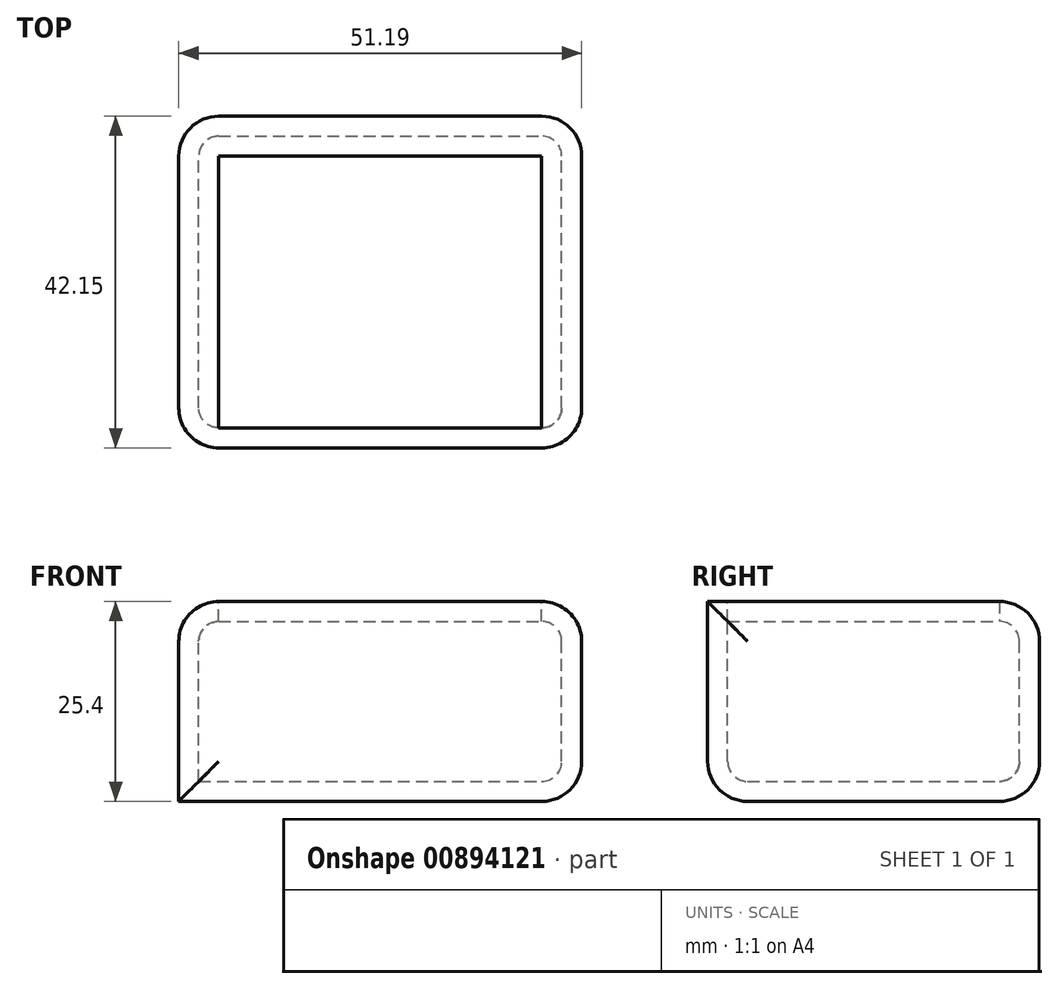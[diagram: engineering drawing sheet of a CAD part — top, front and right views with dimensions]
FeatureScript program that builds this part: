
annotation { "Feature Type Name" : "Feature", "Feature Type Description" : "" }
export const myFeature = defineFeature(function(context is Context, id is Id, definition is map)
    precondition{}
    {
        {
            var Q0;
            Q0=qCreatedBy(makeId("Top.planeOp"),FACE);
            var sketch = newSketch(context, id + "F0", { "sketchPlane" : qUnion([Q0])});
            skLineSegment(sketch, "E0.bottom", {"start": v(-27.28, -21.54) * mm, "end": v(23.9, -21.54) * mm});
            skLineSegment(sketch, "E0.top", {"start": v(-27.28, 20.6) * mm, "end": v(23.9, 20.6) * mm});
            skLineSegment(sketch, "E0.left", {"start": v(-27.28, -21.54) * mm, "end": v(-27.28, 20.6) * mm});
            skLineSegment(sketch, "E0.right", {"start": v(23.9, -21.54) * mm, "end": v(23.9, 20.6) * mm});
            skSolve(sketch);
        }
        {
            var Q0;
            Q0 = qSketchRegion(id + "F0", true);
            extrude(context, id + "F1", {"entities" : qUnion([Q0]), "depth" : 25.4 * mm, "offsetDistance" : 25.4 * mm});
        }
        {
            var Q0;
            Q0=makeQuery(id+"F1.opExtrude","CAP_EDGE",EDGE,{"disambiguationData":[OSD([sQuery(id+"F0.wireOp",EDGE,"E0.top")])],"isStart":false});
            var Q1;
            Q1=makeQuery(id+"F1.opExtrude","CAP_EDGE",EDGE,{"disambiguationData":[OSD([sQuery(id+"F0.wireOp",EDGE,"E0.left")])],"isStart":false});
            var Q2;
            Q2=makeQuery(id+"F1.opExtrude","CAP_EDGE",EDGE,{"disambiguationData":[OSD([sQuery(id+"F0.wireOp",EDGE,"E0.right")])],"isStart":false});
            var Q3;
            Q3=makeQuery(id+"F1.opExtrude","CAP_EDGE",EDGE,{"disambiguationData":[OSD([sQuery(id+"F0.wireOp",EDGE,"E0.right")])],"isStart":true});
            var Q4;
            Q4=makeQuery(id+"F1.opExtrude","SWEPT_EDGE",EDGE,{"disambiguationData":[OSD([sQuery(id+"F0.wireOp",EDGE,"E0.top"),sQuery(id+"F0.wireOp",EDGE,"E0.right")])]});
            var Q5;
            Q5=makeQuery(id+"F1.opExtrude","SWEPT_EDGE",EDGE,{"disambiguationData":[OSD([sQuery(id+"F0.wireOp",EDGE,"E0.bottom"),sQuery(id+"F0.wireOp",EDGE,"E0.right")])]});
            var Q6;
            Q6=makeQuery(id+"F1.opExtrude","SWEPT_EDGE",EDGE,{"disambiguationData":[OSD([sQuery(id+"F0.wireOp",EDGE,"E0.top"),sQuery(id+"F0.wireOp",EDGE,"E0.left")])]});
            var Q7;
            Q7=makeQuery(id+"F1.opExtrude","CAP_EDGE",EDGE,{"disambiguationData":[OSD([sQuery(id+"F0.wireOp",EDGE,"E0.bottom")])],"isStart":true});
            var Q8;
            Q8=makeQuery(id+"F1.opExtrude","SWEPT_EDGE",EDGE,{"disambiguationData":[OSD([sQuery(id+"F0.wireOp",EDGE,"E0.bottom"),sQuery(id+"F0.wireOp",EDGE,"E0.left")])]});
            var Q9;
            Q9=makeQuery(id+"F1.opExtrude","CAP_EDGE",EDGE,{"disambiguationData":[OSD([sQuery(id+"F0.wireOp",EDGE,"E0.top")])],"isStart":true});
            fillet(context, id + "F2", {"entities" : qUnion([Q0, Q1, Q2, Q3, Q4, Q5, Q6, Q7, Q8, Q9]), "radius" : 5.08 * mm, "tangentPropagation" : true, "allowEdgeOverflow" : false});
        }
        {
            var Q0;
            Q0=makeQuery(id+"F1.opExtrude","CAP_FACE",FACE,{"disambiguationData":[OSD([sQuery(id+"F0.wireOp",EDGE,"E0.bottom"),sQuery(id+"F0.wireOp",EDGE,"E0.top"),sQuery(id+"F0.wireOp",EDGE,"E0.left"),sQuery(id+"F0.wireOp",EDGE,"E0.right")])],"isStart":false});
            shell(context, id + "F3", {"entities" : qUnion([Q0]), "thickness" : 2.54 * mm});
        }
    });
